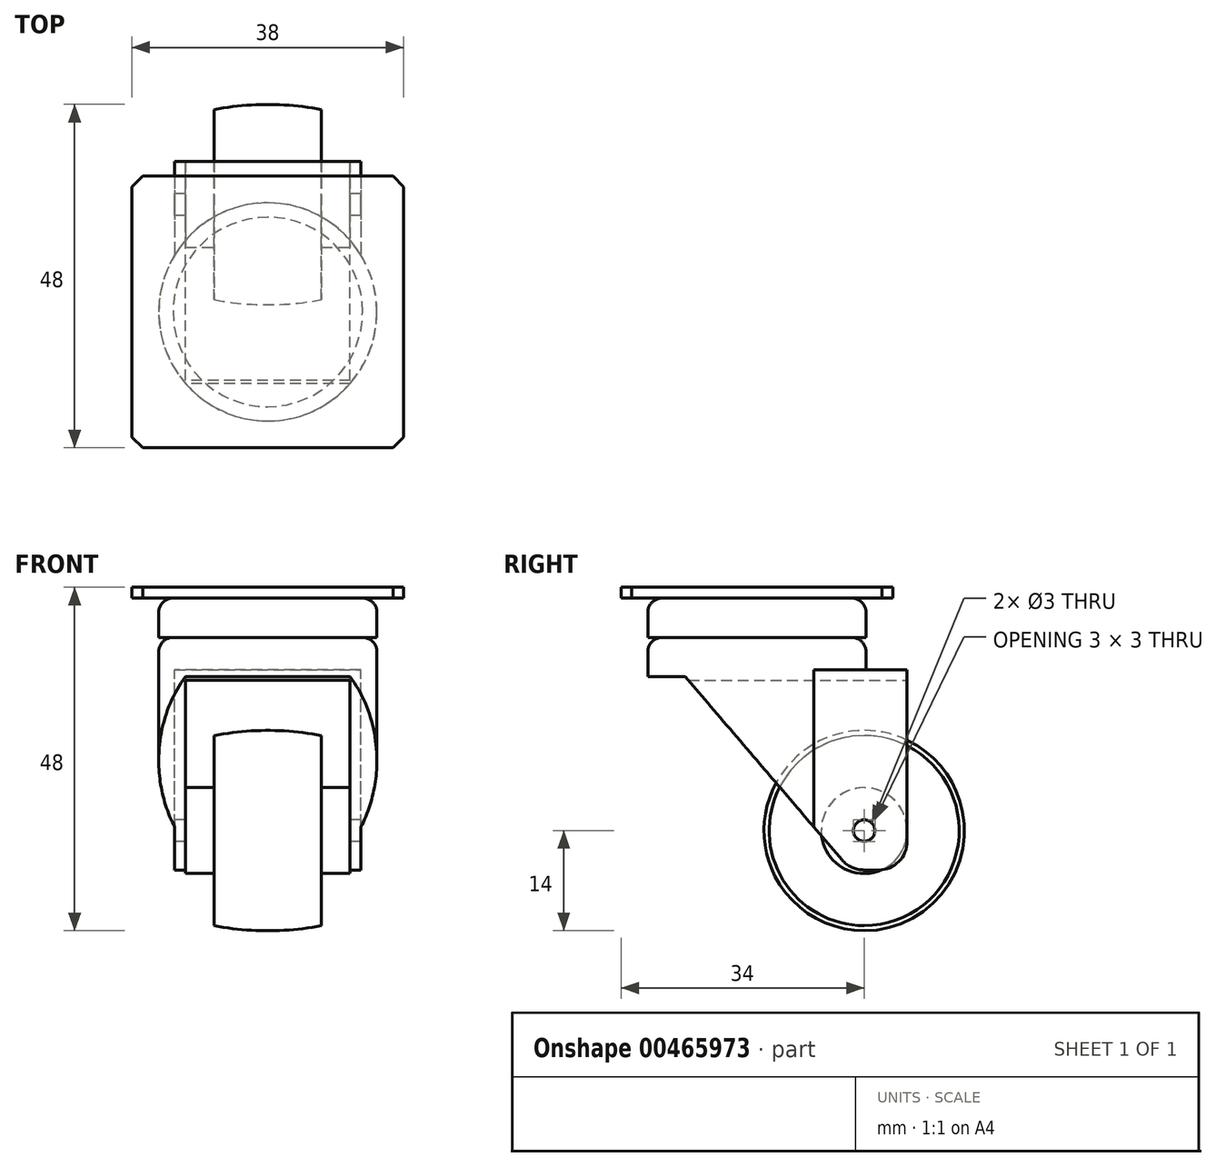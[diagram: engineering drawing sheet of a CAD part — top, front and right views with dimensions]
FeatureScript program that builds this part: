
annotation { "Feature Type Name" : "Feature", "Feature Type Description" : "" }
export const myFeature = defineFeature(function(context is Context, id is Id, definition is map)
    precondition{}
    {
        {
            var Q0;
            Q0=qCreatedBy(makeId("Top.planeOp"),FACE);
            var sketch = newSketch(context, id + "F0", { "sketchPlane" : qUnion([Q0])});
            skLineSegment(sketch, "E0.bottom", {"start": v(-19, 19) * mm, "end": v(19, 19) * mm});
            skLineSegment(sketch, "E0.top", {"start": v(-19, -19) * mm, "end": v(19, -19) * mm});
            skLineSegment(sketch, "E0.left", {"start": v(-19, 19) * mm, "end": v(-19, -19) * mm});
            skLineSegment(sketch, "E0.right", {"start": v(19, 19) * mm, "end": v(19, -19) * mm});
            skSolve(sketch);
        }
        {
            var Q0;
            Q0 = qSketchRegion(id + "F0", true);
            extrude(context, id + "F1", {"entities" : qUnion([Q0]), "depth" : 1.5 * mm, "offsetDistance" : 25 * mm});
        }
        {
            var Q0;
            Q0=makeQuery(id+"F1.opExtrude","SWEPT_EDGE",EDGE,{"disambiguationData":[OSD([sQuery(id+"F0.wireOp",EDGE,"E0.bottom"),sQuery(id+"F0.wireOp",EDGE,"E0.left")])]});
            var Q1;
            Q1=makeQuery(id+"F1.opExtrude","SWEPT_EDGE",EDGE,{"disambiguationData":[OSD([sQuery(id+"F0.wireOp",EDGE,"E0.top"),sQuery(id+"F0.wireOp",EDGE,"E0.left")])]});
            var Q2;
            Q2=makeQuery(id+"F1.opExtrude","SWEPT_EDGE",EDGE,{"disambiguationData":[OSD([sQuery(id+"F0.wireOp",EDGE,"E0.top"),sQuery(id+"F0.wireOp",EDGE,"E0.right")])]});
            var Q3;
            Q3=makeQuery(id+"F1.opExtrude","SWEPT_EDGE",EDGE,{"disambiguationData":[OSD([sQuery(id+"F0.wireOp",EDGE,"E0.bottom"),sQuery(id+"F0.wireOp",EDGE,"E0.right")])]});
            chamfer(context, id + "F2", {"entities" : qUnion([Q0, Q1, Q2, Q3]), "width" : 1.5 * mm, "tangentPropagation" : true});
        }
        {
            var Q0;
            Q0=qCreatedBy(makeId("Right.planeOp"),FACE);
            var sketch = newSketch(context, id + "F3", { "sketchPlane" : qUnion([Q0])});
            skLineSegment(sketch, "E1", {"start": v(0, 21.05) * mm, "end": v(0, -22.11) * mm, "construction": true});
            skLineSegment(sketch, "E2", {"start": v(0, 0) * mm, "end": v(13.25, 0) * mm});
            skLineSegment(sketch, "E3", {"start": v(15.25, -2) * mm, "end": v(15.25, -5.5) * mm});
            skLineSegment(sketch, "E4", {"start": v(15.25, -5.5) * mm, "end": v(13.25, -5.5) * mm});
            skLineSegment(sketch, "E5", {"start": v(0, -11) * mm, "end": v(0, 0) * mm});
            skPoint(sketch, "E6.visualSharp", {"position": v(15.25, 0) * mm});
            skArc(sketch, "E6.filletArc", {"start": v(15.25, -2) * mm, "mid": v(14.66, -0.59) * mm, "end": v(13.25, 0) * mm});
            skLineSegment(sketch, "E7", {"start": v(0, -11) * mm, "end": v(15.25, -11) * mm});
            skLineSegment(sketch, "E8", {"start": v(15.25, -11) * mm, "end": v(15.25, -7.5) * mm});
            skArc(sketch, "E9", {"start": v(15.25, -7.5) * mm, "mid": v(14.66, -6.09) * mm, "end": v(13.25, -5.5) * mm});
            skSolve(sketch);
        }
        {
            var Q0;
            Q0 = qSketchRegion(id + "F3", true);
            var Q1;
            Q1=sQuery(id+"F3.wireOp",EDGE,"E1");
            revolve(context, id + "F4", {"operationType" : NewBodyOperationType.ADD, "entities" : qUnion([Q0]), "axis" : qUnion([Q1]), "revolveType" : RevolveType.FULL});
        }
        {
            var Q0;
            Q0=qCreatedBy(makeId("Right.planeOp"),FACE);
            var sketch = newSketch(context, id + "F5", { "sketchPlane" : qUnion([Q0])});
            skLineSegment(sketch, "E10", {"start": v(-10, -11) * mm, "end": v(11.9, -36.6) * mm});
            skLineSegment(sketch, "E11", {"start": v(14.94, -38) * mm, "end": v(17, -38) * mm});
            skLineSegment(sketch, "E12", {"start": v(21, -34) * mm, "end": v(21, -10) * mm});
            skLineSegment(sketch, "E13", {"start": v(21, -10) * mm, "end": v(-10, -10) * mm});
            skLineSegment(sketch, "E14", {"start": v(-10, -11) * mm, "end": v(-10, -9.98) * mm});
            skCircle(sketch, "E15", {"center": v(15, -32.5) * mm, "radius": 1.5 * mm});
            skPoint(sketch, "E16.visualSharp", {"position": v(13.1, -38) * mm});
            skArc(sketch, "E16.filletArc", {"start": v(11.9, -36.6) * mm, "mid": v(13.27, -37.63) * mm, "end": v(14.94, -38) * mm});
            skPoint(sketch, "E17.visualSharp", {"position": v(21, -38) * mm});
            skArc(sketch, "E17.filletArc", {"start": v(17, -38) * mm, "mid": v(19.83, -36.83) * mm, "end": v(21, -34) * mm});
            skSolve(sketch);
        }
        {
            var Q0;
            Q0 = qSketchRegion(id + "F5", true);
            extrude(context, id + "F6", {"entities" : qUnion([Q0]), "operationType" : NewBodyOperationType.ADD, "depth" : 15.25 * mm, "offsetDistance" : 25 * mm, "hasSecondDirection" : true, "secondDirectionOppositeDirection" : true, "secondDirectionDepth" : 15.25 * mm});
        }
        {
            var Q0;
            {var subQ0=sQuery(id+"F5.wireOp",EDGE,"E12");var subQ1=sQuery(id+"F5.wireOp",EDGE,"E14");var subQ2=sQuery(id+"F5.wireOp",EDGE,"E13");var subQ3=sQuery(id+"F5.wireOp",EDGE,"E11");var subQ4=sQuery(id+"F5.wireOp",EDGE,"E10");var subQ5=makeQuery(id+"F6.opExtrude","SWEPT_FACE",FACE,{"disambiguationData":[OSD([subQ2])]});Q0=makeQuery(id+"F6.boolean.opBoolean","SPLIT",FACE,{"disambiguationData":[TD([makeQuery(id+"F4.opRevolve","SWEPT_FACE",FACE,{"disambiguationData":[OSD([sQuery(id+"F3.wireOp",EDGE,"E8")])]}),makeQuery(id+"F6.opExtrude","CAP_FACE",FACE,{"disambiguationData":[OSD([subQ4,subQ3,subQ0,subQ2,subQ1])],"isStart":true}),makeQuery(id+"F6.opExtrude","CAP_FACE",FACE,{"disambiguationData":[OSD([subQ4,subQ3,subQ0,subQ2,subQ1])],"isStart":false}),makeQuery(id+"F6.opExtrude","SWEPT_FACE",FACE,{"disambiguationData":[OSD([subQ0])]}),subQ5])],"derivedFrom":subQ5});}
            var sketch = newSketch(context, id + "F7", { "sketchPlane" : qUnion([Q0])});
            skLineSegment(sketch, "E18", {"start": v(-22.5, -19) * mm, "end": v(22.5, -19) * mm});
            skLineSegment(sketch, "E19", {"start": v(-13, 21) * mm, "end": v(-13, 7.97) * mm});
            skLineSegment(sketch, "E20", {"start": v(13, 21) * mm, "end": v(13, 7.97) * mm});
            skArc(sketch, "E21", {"start": v(-13, 7.97) * mm, "mid": v(0, -15.25) * mm, "end": v(13, 7.97) * mm});
            skLineSegment(sketch, "E22", {"start": v(-13, 21) * mm, "end": v(-22.5, 21) * mm});
            skLineSegment(sketch, "E23", {"start": v(-22.5, 21) * mm, "end": v(-22.5, -19) * mm});
            skLineSegment(sketch, "E24", {"start": v(13, 21) * mm, "end": v(22.5, 21) * mm});
            skLineSegment(sketch, "E25", {"start": v(22.5, 21) * mm, "end": v(22.5, -19) * mm});
            skSolve(sketch);
        }
        {
            var Q0;
            Q0 = qSketchRegion(id + "F7", true);
            extrude(context, id + "F8", {"entities" : qUnion([Q0]), "operationType" : NewBodyOperationType.REMOVE, "oppositeDirection" : true, "depth" : 30 * mm, "offsetDistance" : 25 * mm});
        }
        {
            var Q0;
            Q0=makeQuery(id+"F6.opExtrude","SWEPT_FACE",FACE,{"disambiguationData":[OSD([sQuery(id+"F5.wireOp",EDGE,"E12")])]});
            var sketch = newSketch(context, id + "F9", { "sketchPlane" : qUnion([Q0])});
            skLineSegment(sketch, "E26.bottom", {"start": v(-11.5, -11.5) * mm, "end": v(11.5, -11.5) * mm});
            skLineSegment(sketch, "E26.top", {"start": v(-11.5, -46.5) * mm, "end": v(11.5, -46.5) * mm});
            skLineSegment(sketch, "E26.left", {"start": v(-11.5, -11.5) * mm, "end": v(-11.5, -46.5) * mm});
            skLineSegment(sketch, "E26.right", {"start": v(11.5, -11.5) * mm, "end": v(11.5, -46.5) * mm});
            skSolve(sketch);
        }
        {
            var Q0;
            Q0 = qSketchRegion(id + "F9", true);
            extrude(context, id + "F10", {"entities" : qUnion([Q0]), "operationType" : NewBodyOperationType.REMOVE, "endBound" : BoundingType.THROUGH_ALL, "oppositeDirection" : true, "depth" : 25 * mm, "offsetDistance" : 25 * mm});
        }
        {
            var Q0;
            Q0=qCreatedBy(makeId("Front.planeOp"),FACE);
            cPlane(context, id + "F11", {"entities" : qUnion([Q0]), "cplaneType" : CPlaneType.OFFSET, "offset" : 15 * mm, "oppositeDirection" : true, "width" : 150 * mm, "height" : 150 * mm});
        }
        {
            var Q0;
            Q0=qCreatedBy(id+"F11.planeOp",FACE);
            var sketch = newSketch(context, id + "F12", { "sketchPlane" : qUnion([Q0])});
            skLineSegment(sketch, "E27", {"start": v(13.92, -32.5) * mm, "end": v(-13.16, -32.5) * mm, "construction": true});
            skLineSegment(sketch, "E28", {"start": v(11.5, -26.5) * mm, "end": v(7.5, -26.5) * mm});
            skLineSegment(sketch, "E29", {"start": v(7.5, -26.5) * mm, "end": v(7.5, -19.22) * mm});
            skLineSegment(sketch, "E30", {"start": v(7.5, -18.5) * mm, "end": v(-7.5, -18.5) * mm, "construction": true});
            skLineSegment(sketch, "E31", {"start": v(-7.5, -19.22) * mm, "end": v(-7.5, -26.5) * mm});
            skLineSegment(sketch, "E32", {"start": v(-7.5, -26.5) * mm, "end": v(-11.5, -26.5) * mm});
            skLineSegment(sketch, "E33", {"start": v(11.5, -26.5) * mm, "end": v(11.5, -32.5) * mm});
            skLineSegment(sketch, "E34", {"start": v(11.5, -32.5) * mm, "end": v(-11.51, -32.5) * mm});
            skLineSegment(sketch, "E35", {"start": v(-11.51, -32.5) * mm, "end": v(-11.5, -26.5) * mm});
            skArc(sketch, "E36", {"start": v(7.5, -19.22) * mm, "mid": v(0, -18.5) * mm, "end": v(-7.5, -19.22) * mm});
            skPoint(sketch, "E36.centerSnap0", {"position": v(0, -32.5) * mm});
            skSolve(sketch);
        }
        {
            var Q0;
            Q0 = qSketchRegion(id + "F12", true);
            var Q1;
            Q1=sQuery(id+"F12.wireOp",EDGE,"E27");
            revolve(context, id + "F13", {"entities" : qUnion([Q0]), "axis" : qUnion([Q1]), "revolveType" : RevolveType.FULL});
        }
    });
